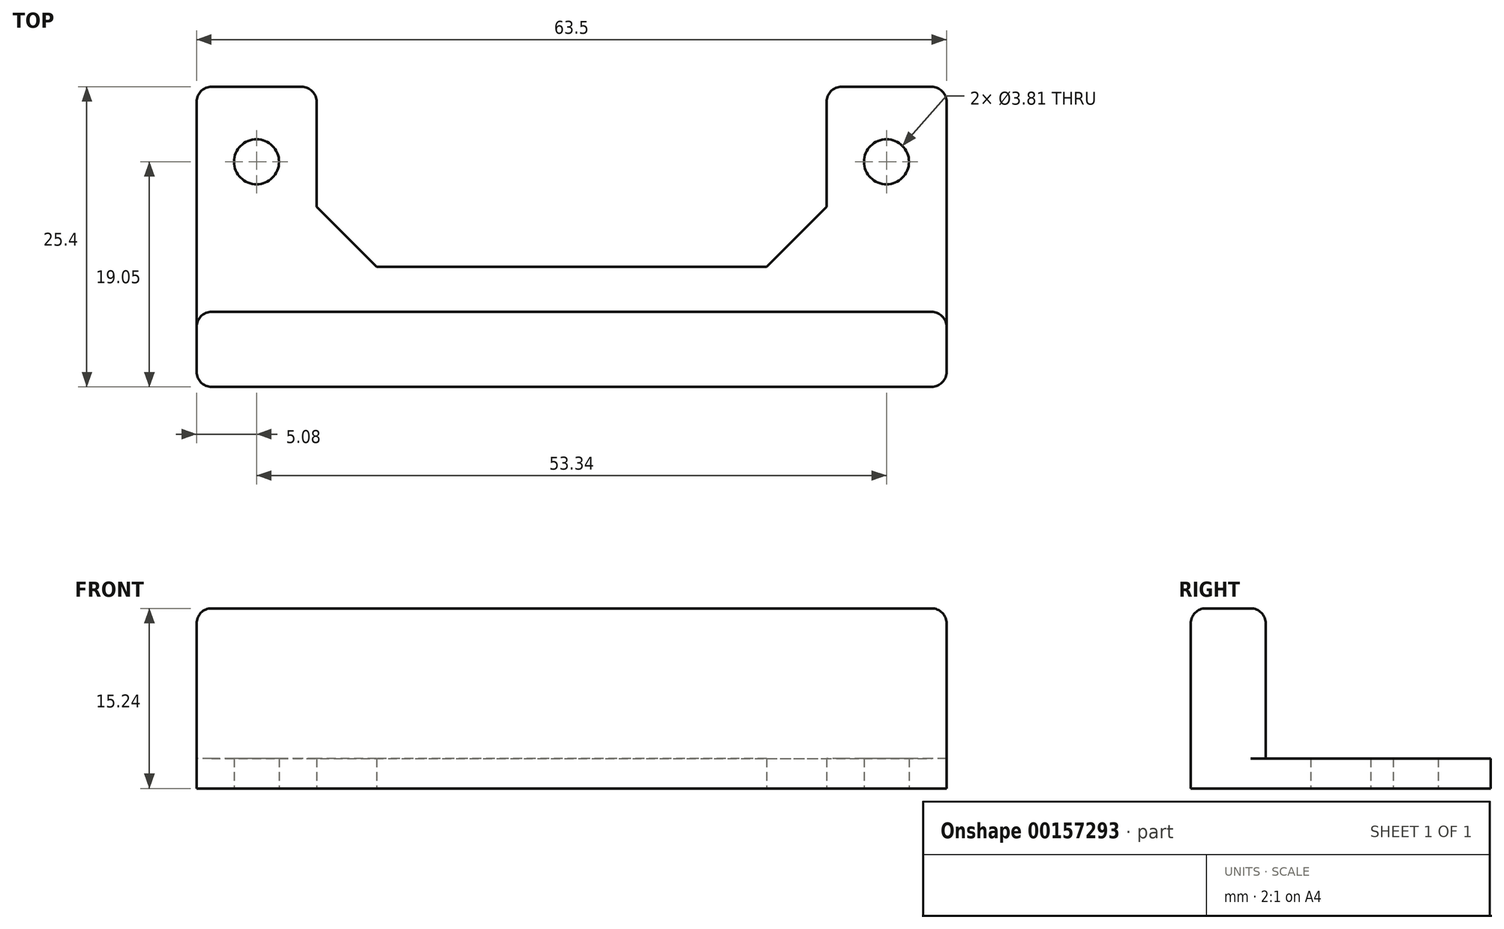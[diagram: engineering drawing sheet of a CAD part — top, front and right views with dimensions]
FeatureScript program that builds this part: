
annotation { "Feature Type Name" : "Feature", "Feature Type Description" : "" }
export const myFeature = defineFeature(function(context is Context, id is Id, definition is map)
    precondition{}
    {
        {
            var Q0;
            Q0=qCreatedBy(makeId("Top.planeOp"),FACE);
            var sketch = newSketch(context, id + "F0", { "sketchPlane" : qUnion([Q0])});
            skLineSegment(sketch, "E0", {"start": v(5.08, 0) * mm, "end": v(68.58, 0) * mm});
            skLineSegment(sketch, "E1", {"start": v(68.58, 0) * mm, "end": v(68.58, 25.4) * mm});
            skLineSegment(sketch, "E2", {"start": v(68.58, 25.4) * mm, "end": v(58.42, 25.4) * mm});
            skLineSegment(sketch, "E3", {"start": v(58.42, 25.4) * mm, "end": v(58.42, 15.24) * mm});
            skLineSegment(sketch, "E4", {"start": v(53.34, 10.16) * mm, "end": v(20.32, 10.16) * mm});
            skLineSegment(sketch, "E5", {"start": v(15.24, 15.24) * mm, "end": v(15.24, 25.4) * mm});
            skLineSegment(sketch, "E6", {"start": v(15.24, 25.4) * mm, "end": v(5.08, 25.4) * mm});
            skLineSegment(sketch, "E7", {"start": v(5.08, 25.4) * mm, "end": v(5.08, 0) * mm});
            skCircle(sketch, "E8", {"center": v(10.16, 19.05) * mm, "radius": 1.9 * mm});
            skCircle(sketch, "E9", {"center": v(63.5, 19.05) * mm, "radius": 1.9 * mm});
            skLineSegment(sketch, "E10", {"start": v(20.32, 10.16) * mm, "end": v(15.24, 15.24) * mm});
            skLineSegment(sketch, "E11", {"start": v(53.34, 10.16) * mm, "end": v(58.42, 15.24) * mm});
            skSolve(sketch);
        }
        {
            var Q0;
            Q0 = qSketchRegion(id + "F0", true);
            extrude(context, id + "F1", {"entities" : qUnion([Q0]), "depth" : 2.54 * mm});
        }
        {
            var Q0;
            Q0=makeQuery(id+"F1.opExtrude","CAP_FACE",FACE,{"disambiguationData":[OSD([sQuery(id+"F0.wireOp",EDGE,"E0"),sQuery(id+"F0.wireOp",EDGE,"E1"),sQuery(id+"F0.wireOp",EDGE,"E2"),sQuery(id+"F0.wireOp",EDGE,"E3"),sQuery(id+"F0.wireOp",EDGE,"E4"),sQuery(id+"F0.wireOp",EDGE,"E5"),sQuery(id+"F0.wireOp",EDGE,"E6"),sQuery(id+"F0.wireOp",EDGE,"E7"),sQuery(id+"F0.wireOp",EDGE,"E8"),sQuery(id+"F0.wireOp",EDGE,"E9"),sQuery(id+"F0.wireOp",EDGE,"E10"),sQuery(id+"F0.wireOp",EDGE,"E11")])],"isStart":false});
            var sketch = newSketch(context, id + "F2", { "sketchPlane" : qUnion([Q0])});
            skLineSegment(sketch, "E12.bottom", {"start": v(5.08, 0) * mm, "end": v(68.58, 0) * mm});
            skLineSegment(sketch, "E12.top", {"start": v(5.08, 6.35) * mm, "end": v(68.58, 6.35) * mm});
            skLineSegment(sketch, "E12.left", {"start": v(5.08, 0) * mm, "end": v(5.08, 6.35) * mm});
            skLineSegment(sketch, "E12.right", {"start": v(68.58, 0) * mm, "end": v(68.58, 6.35) * mm});
            skSolve(sketch);
        }
        {
            var Q0;
            Q0 = qSketchRegion(id + "F2", true);
            extrude(context, id + "F3", {"entities" : qUnion([Q0]), "operationType" : NewBodyOperationType.ADD, "depth" : 12.7 * mm});
        }
        {
            var Q0;
            Q0=makeQuery(id+"F3.opExtrude","CAP_EDGE",EDGE,{"disambiguationData":[OSD([sQuery(id+"F2.wireOp",EDGE,"E12.bottom")])],"isStart":false});
            var Q1;
            Q1=makeQuery(id+"F3.opExtrude","CAP_EDGE",EDGE,{"disambiguationData":[OSD([sQuery(id+"F2.wireOp",EDGE,"E12.top")])],"isStart":false});
            var Q2;
            Q2=makeQuery(id+"F3.boolean.opBoolean","MERGE",EDGE,{"derivedFrom":[makeQuery(id+"F1.opExtrude","SWEPT_EDGE",EDGE,{"disambiguationData":[OSD([sQuery(id+"F0.wireOp",EDGE,"E0"),sQuery(id+"F0.wireOp",EDGE,"E1")])]}),makeQuery(id+"F3.opExtrude","SWEPT_EDGE",EDGE,{"disambiguationData":[OSD([sQuery(id+"F2.wireOp",EDGE,"E12.bottom"),sQuery(id+"F2.wireOp",EDGE,"E12.right")])]})]});
            var Q3;
            Q3=makeQuery(id+"F3.opExtrude","SWEPT_EDGE",EDGE,{"disambiguationData":[OSD([sQuery(id+"F0.wireOp",EDGE,"E1"),sQuery(id+"F2.wireOp",EDGE,"E12.top"),sQuery(id+"F2.wireOp",EDGE,"E12.right")])]});
            var Q4;
            Q4=makeQuery(id+"F3.opExtrude","CAP_EDGE",EDGE,{"disambiguationData":[OSD([sQuery(id+"F2.wireOp",EDGE,"E12.right")])],"isStart":false});
            var Q5;
            Q5=makeQuery(id+"F3.opExtrude","CAP_EDGE",EDGE,{"disambiguationData":[OSD([sQuery(id+"F2.wireOp",EDGE,"E12.left")])],"isStart":false});
            var Q6;
            Q6=makeQuery(id+"F3.boolean.opBoolean","MERGE",EDGE,{"derivedFrom":[makeQuery(id+"F1.opExtrude","SWEPT_EDGE",EDGE,{"disambiguationData":[OSD([sQuery(id+"F0.wireOp",EDGE,"E0"),sQuery(id+"F0.wireOp",EDGE,"E7")])]}),makeQuery(id+"F3.opExtrude","SWEPT_EDGE",EDGE,{"disambiguationData":[OSD([sQuery(id+"F2.wireOp",EDGE,"E12.bottom"),sQuery(id+"F2.wireOp",EDGE,"E12.left")])]})]});
            var Q7;
            Q7=makeQuery(id+"F3.opExtrude","SWEPT_EDGE",EDGE,{"disambiguationData":[OSD([sQuery(id+"F0.wireOp",EDGE,"E7"),sQuery(id+"F2.wireOp",EDGE,"E12.top"),sQuery(id+"F2.wireOp",EDGE,"E12.left")])]});
            fillet(context, id + "F4", {"entities" : qUnion([Q0, Q1, Q2, Q3, Q4, Q5, Q6, Q7]), "radius" : 1.27 * mm, "tangentPropagation" : true, "allowEdgeOverflow" : false});
        }
        {
            var Q0;
            Q0=makeQuery(id+"F1.opExtrude","SWEPT_EDGE",EDGE,{"disambiguationData":[OSD([sQuery(id+"F0.wireOp",EDGE,"E1"),sQuery(id+"F0.wireOp",EDGE,"E2")])]});
            var Q1;
            Q1=makeQuery(id+"F1.opExtrude","SWEPT_EDGE",EDGE,{"disambiguationData":[OSD([sQuery(id+"F0.wireOp",EDGE,"E2"),sQuery(id+"F0.wireOp",EDGE,"E3")])]});
            var Q2;
            Q2=makeQuery(id+"F1.opExtrude","SWEPT_EDGE",EDGE,{"disambiguationData":[OSD([sQuery(id+"F0.wireOp",EDGE,"E5"),sQuery(id+"F0.wireOp",EDGE,"E6")])]});
            var Q3;
            Q3=makeQuery(id+"F1.opExtrude","SWEPT_EDGE",EDGE,{"disambiguationData":[OSD([sQuery(id+"F0.wireOp",EDGE,"E6"),sQuery(id+"F0.wireOp",EDGE,"E7")])]});
            fillet(context, id + "F5", {"entities" : qUnion([Q0, Q1, Q2, Q3]), "radius" : 1.27 * mm, "tangentPropagation" : true, "allowEdgeOverflow" : false});
        }
    });
